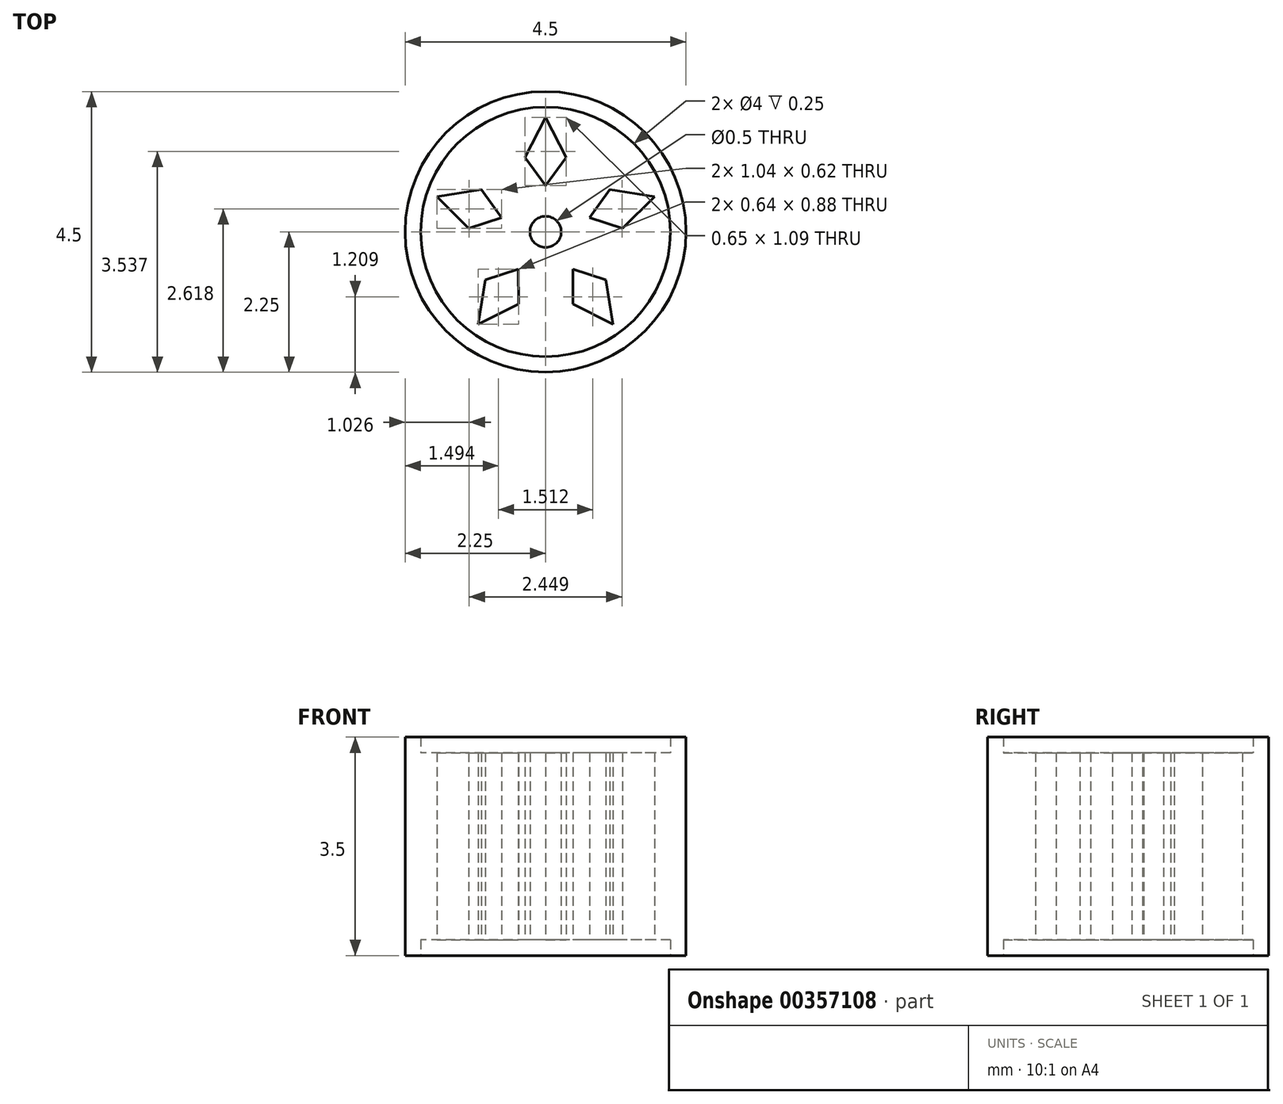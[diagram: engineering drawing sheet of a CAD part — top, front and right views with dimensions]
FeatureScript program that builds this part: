
annotation { "Feature Type Name" : "Feature", "Feature Type Description" : "" }
export const myFeature = defineFeature(function(context is Context, id is Id, definition is map)
    precondition{}
    {
        {
            var Q0;
            Q0=qCreatedBy(makeId("Top.planeOp"),FACE);
            var sketch = newSketch(context, id + "F0", { "sketchPlane" : qUnion([Q0])});
            skCircle(sketch, "E0", {"center": v(0, 0) * mm, "radius": 0.25 * mm});
            skCircle(sketch, "E1", {"center": v(0, 0) * mm, "radius": 2 * mm});
            skCircle(sketch, "E2", {"center": v(0, 0) * mm, "radius": 2.25 * mm});
            skLineSegment(sketch, "E3", {"start": v(0, 1.83) * mm, "end": v(-0.33, 1.2) * mm});
            skLineSegment(sketch, "E4", {"start": v(-0.33, 1.2) * mm, "end": v(0, 0.74) * mm});
            skLineSegment(sketch, "E5.MirrorCS", {"start": v(0, 1.83) * mm, "end": v(0.33, 1.2) * mm});
            skLineSegment(sketch, "E6.MirrorCS", {"start": v(0.33, 1.2) * mm, "end": v(0, 0.74) * mm});
            skLineSegment(sketch, "E7.1.0", {"start": v(-1.74, 0.57) * mm, "end": v(-1.23, 0.06) * mm});
            skLineSegment(sketch, "E7.1.1", {"start": v(-1.23, 0.06) * mm, "end": v(-0.7, 0.23) * mm});
            skLineSegment(sketch, "E7.1.2", {"start": v(-1.03, 0.68) * mm, "end": v(-0.7, 0.23) * mm});
            skLineSegment(sketch, "E7.1.3", {"start": v(-1.74, 0.57) * mm, "end": v(-1.03, 0.68) * mm});
            skLineSegment(sketch, "E7.2.0", {"start": v(-1.08, -1.48) * mm, "end": v(-0.43, -1.16) * mm});
            skLineSegment(sketch, "E7.2.1", {"start": v(-0.43, -1.16) * mm, "end": v(-0.44, -0.6) * mm});
            skLineSegment(sketch, "E7.2.2", {"start": v(-0.96, -0.77) * mm, "end": v(-0.44, -0.6) * mm});
            skLineSegment(sketch, "E7.2.3", {"start": v(-1.08, -1.48) * mm, "end": v(-0.96, -0.77) * mm});
            skLineSegment(sketch, "E7.3.0", {"start": v(1.08, -1.48) * mm, "end": v(0.96, -0.77) * mm});
            skLineSegment(sketch, "E7.3.1", {"start": v(0.96, -0.77) * mm, "end": v(0.44, -0.6) * mm});
            skLineSegment(sketch, "E7.3.2", {"start": v(0.43, -1.16) * mm, "end": v(0.44, -0.6) * mm});
            skLineSegment(sketch, "E7.3.3", {"start": v(1.08, -1.48) * mm, "end": v(0.43, -1.16) * mm});
            skLineSegment(sketch, "E7.4.0", {"start": v(1.74, 0.57) * mm, "end": v(1.03, 0.68) * mm});
            skLineSegment(sketch, "E7.4.1", {"start": v(1.03, 0.68) * mm, "end": v(0.7, 0.23) * mm});
            skLineSegment(sketch, "E7.4.2", {"start": v(1.23, 0.06) * mm, "end": v(0.7, 0.23) * mm});
            skLineSegment(sketch, "E7.4.3", {"start": v(1.74, 0.57) * mm, "end": v(1.23, 0.06) * mm});
            skSolve(sketch);
        }
        {
            var Q0;
            Q0=makeQuery(id+"F0.imprint","IMPRINT",FACE,{"disambiguationData":[TD([[makeQuery(id+"F0.imprint","IMPRINT",EDGE,{"derivedFrom":sQuery(id+"F0.wireOp",EDGE,"E0")}),-1.0]])]});
            extrude(context, id + "F1", {"entities" : qUnion([Q0]), "endBound" : BoundingType.SYMMETRIC, "depth" : 3 * mm});
        }
        {
            var Q0;
            Q0=makeQuery(id+"F0.imprint","IMPRINT",FACE,{"disambiguationData":[TD([[makeQuery(id+"F0.imprint","IMPRINT",EDGE,{"derivedFrom":sQuery(id+"F0.wireOp",EDGE,"E1")}),-1.0]])]});
            extrude(context, id + "F2", {"entities" : qUnion([Q0]), "operationType" : NewBodyOperationType.ADD, "endBound" : BoundingType.SYMMETRIC, "depth" : 3.5 * mm});
        }
    });
